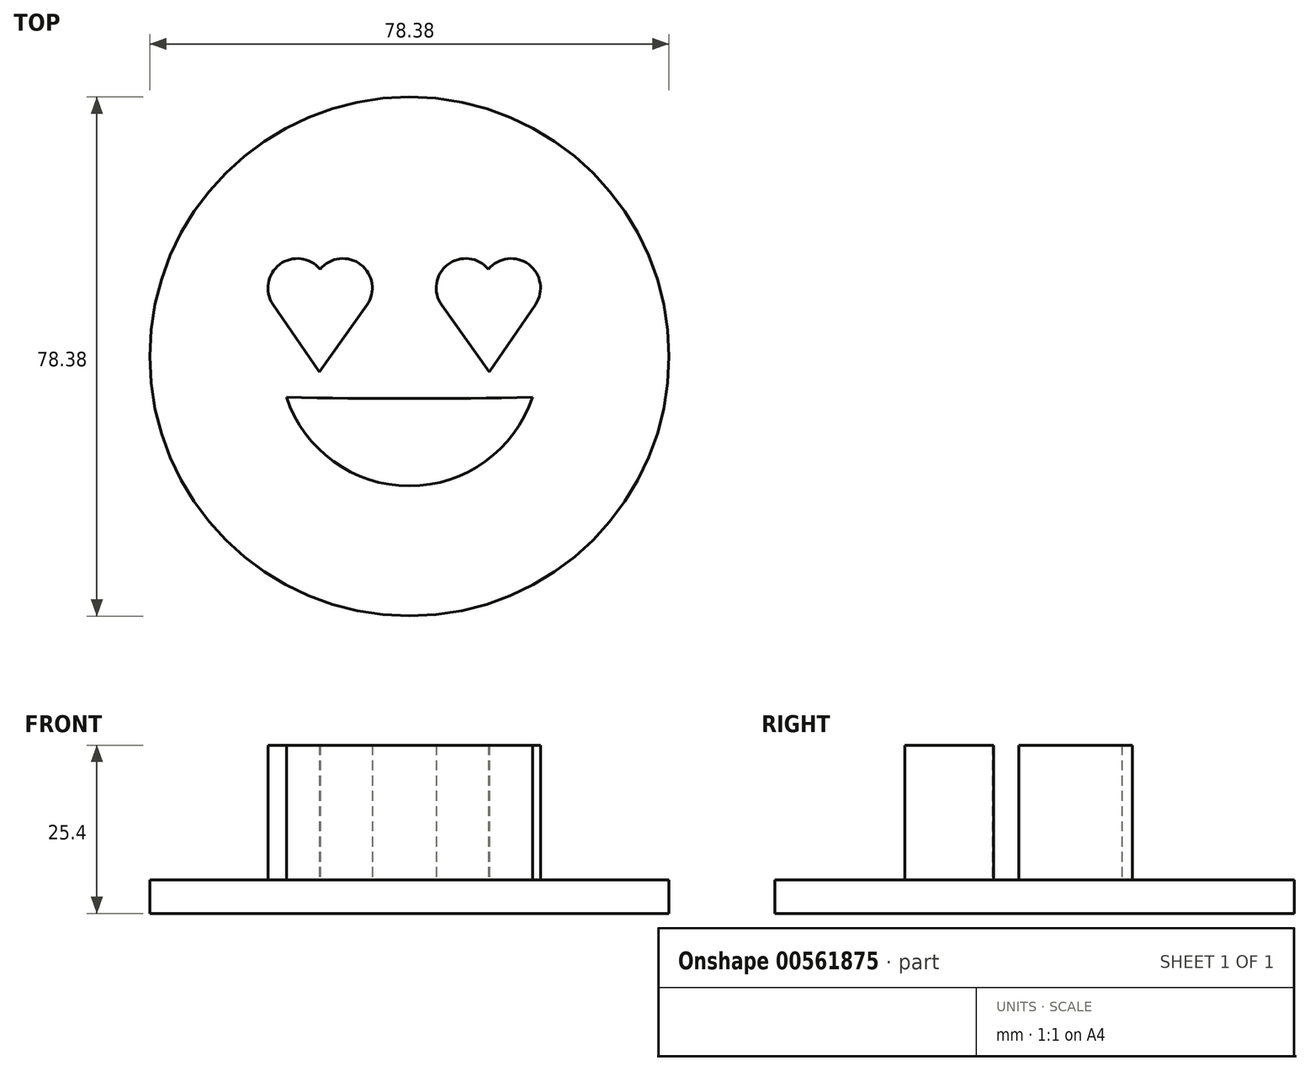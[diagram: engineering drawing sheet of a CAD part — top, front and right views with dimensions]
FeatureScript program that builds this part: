
annotation { "Feature Type Name" : "Feature", "Feature Type Description" : "" }
export const myFeature = defineFeature(function(context is Context, id is Id, definition is map)
    precondition{}
    {
        {
            var Q0;
            Q0=qCreatedBy(makeId("Top.planeOp"),FACE);
            var sketch = newSketch(context, id + "F0", { "sketchPlane" : qUnion([Q0])});
            skCircle(sketch, "E0", {"center": v(-25.4, 12.7) * mm, "radius": 4.45 * mm});
            skCircle(sketch, "E1.MirrorC", {"center": v(-18.54, 12.7) * mm, "radius": 4.45 * mm});
            skLineSegment(sketch, "E2", {"start": v(-29.07, 10.2) * mm, "end": v(-22.12, 0) * mm});
            skLineSegment(sketch, "E3", {"start": v(-22.12, 0) * mm, "end": v(-14.92, 10.12) * mm});
            skCircle(sketch, "E4.MirrorC", {"center": v(6.86, 12.7) * mm, "radius": 4.45 * mm});
            skCircle(sketch, "E5.MirrorC", {"center": v(0, 12.7) * mm, "radius": 4.45 * mm});
            skLineSegment(sketch, "E6.MirrorCS", {"start": v(10.53, 10.2) * mm, "end": v(3.57, 0) * mm});
            skLineSegment(sketch, "E7.MirrorCS", {"start": v(3.57, 0) * mm, "end": v(-3.62, 10.12) * mm});
            skArc(sketch, "E8", {"start": v(-27.05, -3.8) * mm, "mid": v(-8.49, -4) * mm, "end": v(10.08, -3.8) * mm});
            skArc(sketch, "E9", {"start": v(-27.05, -3.81) * mm, "mid": v(-8.49, -17.2) * mm, "end": v(10.08, -3.81) * mm});
            skSolve(sketch);
        }
        {
            var Q0;
            Q0 = qSketchRegion(id + "F0", true);
            extrude(context, id + "F1", {"entities" : qUnion([Q0]), "depth" : 25.4 * mm, "offsetDistance" : 25.4 * mm});
        }
        {
            var Q0;
            Q0=qCreatedBy(makeId("Top.planeOp"),FACE);
            var sketch = newSketch(context, id + "F2", { "sketchPlane" : qUnion([Q0])});
            skCircle(sketch, "E10", {"center": v(-8.49, 2.35) * mm, "radius": 39.2 * mm});
            skSolve(sketch);
        }
        {
            var Q0;
            Q0=makeQuery(id+"F2.imprint","IMPRINT",FACE,{"disambiguationData":[TD([[makeQuery(id+"F2.imprint","IMPRINT",EDGE,{"derivedFrom":sQuery(id+"F2.wireOp",EDGE,"E10")}),1.0]])]});
            extrude(context, id + "F3", {"entities" : qUnion([Q0]), "operationType" : NewBodyOperationType.ADD, "depth" : 5.08 * mm, "offsetDistance" : 25.4 * mm});
        }
    });
